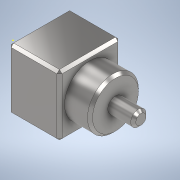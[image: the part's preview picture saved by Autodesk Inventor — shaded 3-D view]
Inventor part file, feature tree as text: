
AUTODESK INVENTOR PART (.ipt)
format: ipt  version: 2021 (Build 250183000, 183)  size: 171,520 bytes
history: native  units: mm
features: sketch x5, extrude x3, chamfer x1
ambient origin geometry x8: Origin, YZ Plane, XZ Plane, XY Plane, X Axis, Y Axis, Z Axis, Center Point
bodies: Solid1 (feature_tree)
feature tree (9):
  sketch  "Sketch1"  dims[d2=20.0mm d3=0.0mm d7=10.0mm d8=0.0mm]
  extrude  "Extrusion1"  Depth=10.0mm TaperAngle=0.0deg
  extrude  "Extrusion2"  Depth=10.0mm TaperAngle=45.0deg
  extrude  "Extrusion3"  [1 undecoded]
  chamfer  "Chamfer1"  [1 undecoded]
  sketch  "Sketch5"
  sketch  "Sketch2"  dims[d10=10.0mm d11=0.0mm d12=1.0mm d13=2.0mm d14=45.0deg]
  sketch  "Sketch3"  dims[d9=0.5mm]
  sketch  "Sketch4"
note: 2 required parameter values undecoded (feature->parameter linkage not recoverable at this tier; creation-order binding heuristic only, values carry confidence <= 0.55)
